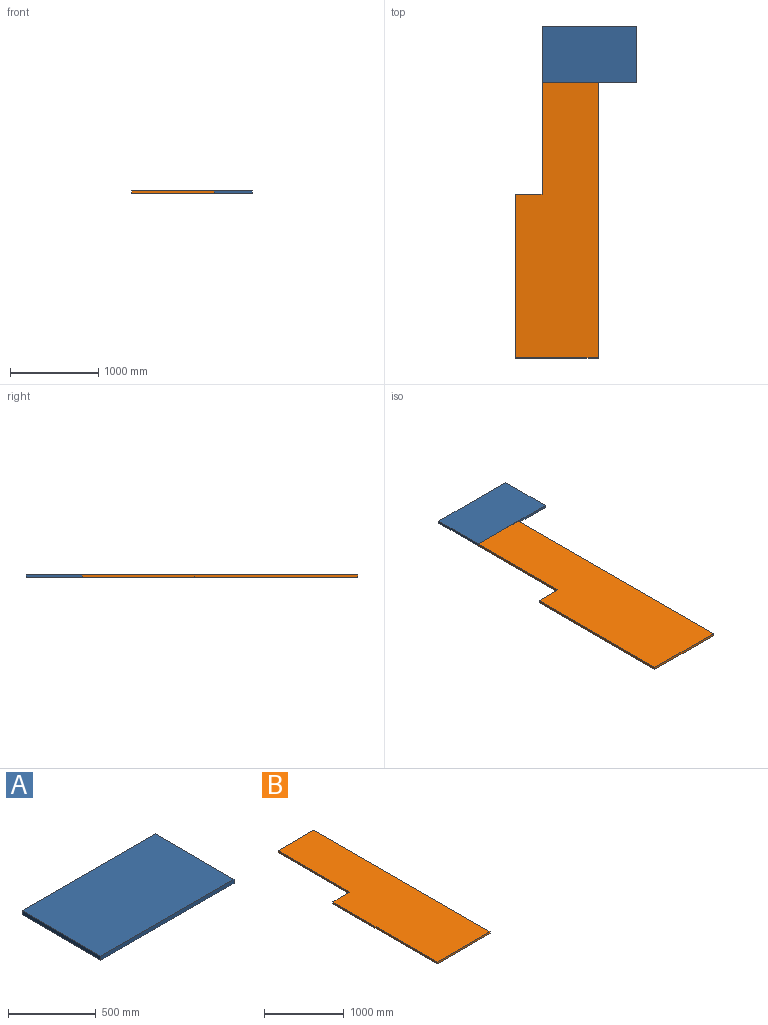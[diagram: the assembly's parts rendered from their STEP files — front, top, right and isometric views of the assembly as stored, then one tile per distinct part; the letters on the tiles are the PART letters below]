
ASSEMBLY  parts=2 mates=1
PART A: 6 faces, bbox 1070x635x28 mm
  f0: plane 635x28mm, normal (-1,0,0), area 17780mm2, adj f1,f3,f4,f5
  f1: plane 1070x28mm, normal (0,-1,0), area 29960mm2, adj f0,f2,f4,f5
  f2: plane 635x28mm, normal (1,0,0), area 17780mm2, adj f1,f3,f4,f5
  f3: plane 1070x28mm, normal (0,1,0), area 29960mm2, adj f0,f2,f4,f5
  f4: plane 1070x635mm, normal (0,0,1), area 679450mm2, adj f0,f1,f2,f3
  f5: plane 1070x635mm, normal (0,0,-1), area 679450mm2, adj f0,f1,f2,f3
PART B: 8 faces, bbox 935x3125x28 mm
  f0: plane 3125x28mm, normal (1,0,0), area 87500mm2, adj f1,f5,f6,f7
  f1: plane 635x28mm, normal (0,1,0), area 17780mm2, adj f0,f2,f6,f7
  f2: plane 1272x28mm, normal (-1,0,0), area 35616mm2, adj f1,f3,f6,f7
  f3: plane 300x28mm, normal (0,1,0), area 8400mm2, adj f2,f4,f6,f7
  f4: plane 1853x28mm, normal (-1,0,0), area 51884mm2, adj f3,f5,f6,f7
  f5: plane 935x28mm, normal (0,-1,0), area 26180mm2, adj f0,f4,f6,f7
  f6: plane 3125x935mm, normal (0,0,1), area 2540275mm2, adj f0,f1,f2,f3,f4,f5
  f7: plane 3125x935mm, normal (0,0,-1), area 2540275mm2, adj f0,f1,f2,f3,f4,f5
PLACE A t=(-323.32,597.95,701.69)mm
PLACE B t=(-323.32,-674.05,701.69)mm
MATE fastened B.f1 <-> A.f1  axis (0,1,0) through (-323.32,597.95,715.69)mm
